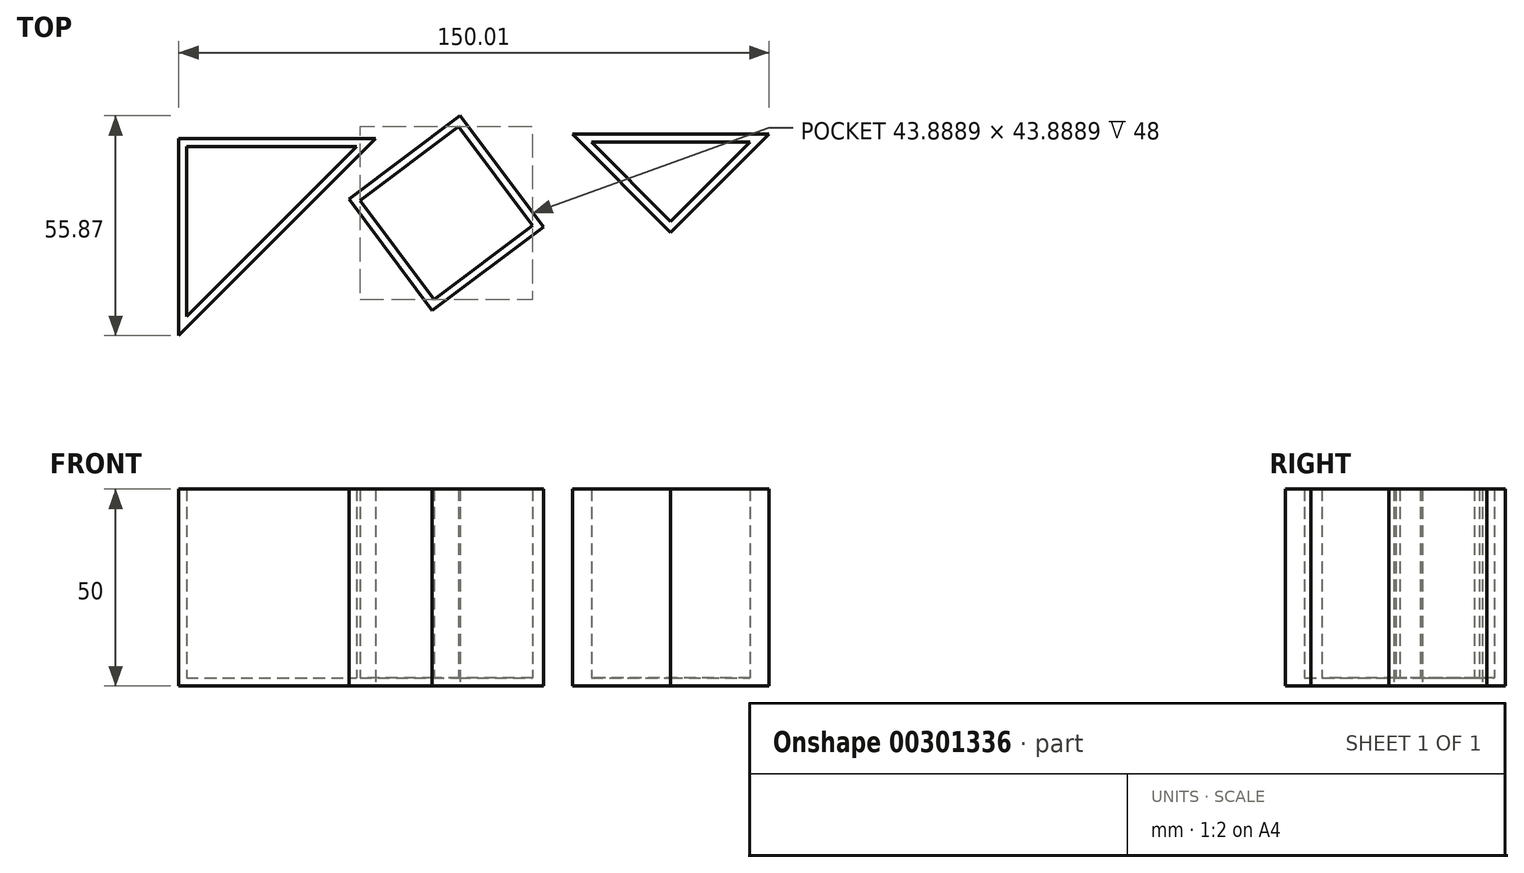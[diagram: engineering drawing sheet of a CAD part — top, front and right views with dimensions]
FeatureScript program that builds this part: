
annotation { "Feature Type Name" : "Feature", "Feature Type Description" : "" }
export const myFeature = defineFeature(function(context is Context, id is Id, definition is map)
    precondition{}
    {
        {
            var Q0;
            Q0=qCreatedBy(makeId("Top.planeOp"),FACE);
            var sketch = newSketch(context, id + "F0", { "sketchPlane" : qUnion([Q0])});
            skLineSegment(sketch, "E0", {"start": v(-123.83, 28.33) * mm, "end": v(-73.83, 28.33) * mm});
            skLineSegment(sketch, "E1", {"start": v(-73.83, 28.33) * mm, "end": v(-123.83, -21.67) * mm});
            skLineSegment(sketch, "E2", {"start": v(-123.83, -21.67) * mm, "end": v(-123.83, 28.33) * mm});
            skLineSegment(sketch, "E3", {"start": v(-23.82, 29.52) * mm, "end": v(1.18, 4.52) * mm});
            skLineSegment(sketch, "E4", {"start": v(1.18, 4.52) * mm, "end": v(26.18, 29.52) * mm});
            skLineSegment(sketch, "E5", {"start": v(26.18, 29.52) * mm, "end": v(-23.82, 29.52) * mm});
            skLineSegment(sketch, "E6", {"start": v(-52.28, 34.2) * mm, "end": v(-31.1, 5.88) * mm});
            skLineSegment(sketch, "E7", {"start": v(-31.1, 5.88) * mm, "end": v(-59.42, -15.3) * mm});
            skLineSegment(sketch, "E8", {"start": v(-59.42, -15.3) * mm, "end": v(-80.6, 13.02) * mm});
            skLineSegment(sketch, "E9", {"start": v(-80.6, 13.02) * mm, "end": v(-52.28, 34.2) * mm});
            skSolve(sketch);
        }
        {
            var Q0;
            Q0=makeQuery(id+"F0.imprint","IMPRINT",FACE,{"disambiguationData":[TD([[makeQuery(id+"F0.imprint","IMPRINT",EDGE,{"derivedFrom":sQuery(id+"F0.wireOp",EDGE,"E0")}),-1.0]])]});
            var Q1;
            Q1=makeQuery(id+"F0.imprint","IMPRINT",FACE,{"disambiguationData":[TD([[makeQuery(id+"F0.imprint","IMPRINT",EDGE,{"derivedFrom":sQuery(id+"F0.wireOp",EDGE,"E6")}),-1.0]])]});
            var Q2;
            Q2=makeQuery(id+"F0.imprint","IMPRINT",FACE,{"disambiguationData":[TD([[makeQuery(id+"F0.imprint","IMPRINT",EDGE,{"derivedFrom":sQuery(id+"F0.wireOp",EDGE,"E3")}),1.0]])]});
            var Q3;
            Q3=makeQuery(id+"F0.imprint","IMPRINT",FACE,{"disambiguationData":[TD([[makeQuery(id+"F0.imprint","IMPRINT",EDGE,{"derivedFrom":sQuery(id+"F0.wireOp",EDGE,"U0t9W74e-d2fm-0y7L-Wo4W-Viqy2OSfyWCx")}),-1.0]])]});
            var Q4;
            Q4=makeQuery(id+"F0.imprint","IMPRINT",FACE,{"disambiguationData":[TD([[makeQuery(id+"F0.imprint","IMPRINT",EDGE,{"derivedFrom":sQuery(id+"F0.wireOp",EDGE,"vE9VVzl6-ql5X-0LAO-jlfI-R53zR6l8MO6H")}),-1.0]])]});
            var Q5;
            Q5=makeQuery(id+"F0.imprint","IMPRINT",FACE,{"disambiguationData":[TD([[makeQuery(id+"F0.imprint","IMPRINT",EDGE,{"derivedFrom":sQuery(id+"F0.wireOp",EDGE,"E3aqfVfO-3GXS-RRkT-9ksH-RdOsN6yz0HLw")}),1.0]])]});
            var Q6;
            Q6=makeQuery(id+"F0.imprint","IMPRINT",FACE,{"disambiguationData":[TD([[makeQuery(id+"F0.imprint","IMPRINT",EDGE,{"derivedFrom":sQuery(id+"F0.wireOp",EDGE,"VYNskEuA-4GyB-tb9B-Ziup-JMWr6APt9W85")}),1.0]])]});
            extrude(context, id + "F1", {"entities" : qUnion([Q0, Q1, Q2, Q3, Q4, Q5, Q6]), "depth" : 50 * mm});
        }
        {
            var Q0;
            Q0=makeQuery(id+"F1.opExtrude","CAP_FACE",FACE,{"disambiguationData":[OSD([sQuery(id+"F0.wireOp",EDGE,"E3"),sQuery(id+"F0.wireOp",EDGE,"E4"),sQuery(id+"F0.wireOp",EDGE,"E5")])],"isStart":false});
            var Q1;
            Q1=makeQuery(id+"F1.opExtrude","CAP_FACE",FACE,{"disambiguationData":[OSD([sQuery(id+"F0.wireOp",EDGE,"E6"),sQuery(id+"F0.wireOp",EDGE,"E7"),sQuery(id+"F0.wireOp",EDGE,"E8"),sQuery(id+"F0.wireOp",EDGE,"E9")])],"isStart":false});
            var Q2;
            Q2=makeQuery(id+"F1.opExtrude","CAP_FACE",FACE,{"disambiguationData":[OSD([sQuery(id+"F0.wireOp",EDGE,"U0t9W74e-d2fm-0y7L-Wo4W-Viqy2OSfyWCx"),sQuery(id+"F0.wireOp",EDGE,"l5eABysS-ceoh-8iuf-PpeE-vS6s1TLCbFWI"),sQuery(id+"F0.wireOp",EDGE,"E0QaZQfB-4Xpq-5Bgw-cTlR-npszS7H3kl96")])],"isStart":false});
            var Q3;
            Q3=makeQuery(id+"F1.opExtrude","CAP_FACE",FACE,{"disambiguationData":[OSD([sQuery(id+"F0.wireOp",EDGE,"VYNskEuA-4GyB-tb9B-Ziup-JMWr6APt9W85"),sQuery(id+"F0.wireOp",EDGE,"yDGDOoxQ-XIjA-0bIi-SbFI-folkbcPP6gBW"),sQuery(id+"F0.wireOp",EDGE,"wXXfwCSN-sh12-jaBQ-n7vz-1KVoKZqagKiN")])],"isStart":false});
            var Q4;
            Q4=makeQuery(id+"F1.opExtrude","CAP_FACE",FACE,{"disambiguationData":[OSD([sQuery(id+"F0.wireOp",EDGE,"vE9VVzl6-ql5X-0LAO-jlfI-R53zR6l8MO6H"),sQuery(id+"F0.wireOp",EDGE,"brwAXKiy-eTeC-tMjD-qWXG-ONUU6GLT5wwo"),sQuery(id+"F0.wireOp",EDGE,"R9jRKI9C-6WjF-pQSB-KoW4-lKQJC9NyH12s")])],"isStart":false});
            var Q5;
            Q5=makeQuery(id+"F1.opExtrude","CAP_FACE",FACE,{"disambiguationData":[OSD([sQuery(id+"F0.wireOp",EDGE,"E3aqfVfO-3GXS-RRkT-9ksH-RdOsN6yz0HLw"),sQuery(id+"F0.wireOp",EDGE,"5vEhzn7P-nudT-upLj-eX0M-MM5x2auK3UX3"),sQuery(id+"F0.wireOp",EDGE,"xqMG9NH0-HU0Y-Y3aC-I93R-zHZWhRLWfdcj"),sQuery(id+"F0.wireOp",EDGE,"CAr3MwZw-DJQw-ILgH-6py0-MOr6O5ZLx3WX")])],"isStart":false});
            var Q6;
            Q6=makeQuery(id+"F1.opExtrude","CAP_FACE",FACE,{"disambiguationData":[OSD([sQuery(id+"F0.wireOp",EDGE,"E0"),sQuery(id+"F0.wireOp",EDGE,"E1"),sQuery(id+"F0.wireOp",EDGE,"E2")])],"isStart":false});
            shell(context, id + "F2", {"entities" : qUnion([Q0, Q1, Q2, Q3, Q4, Q5, Q6]), "thickness" : 2 * mm});
        }
    });
